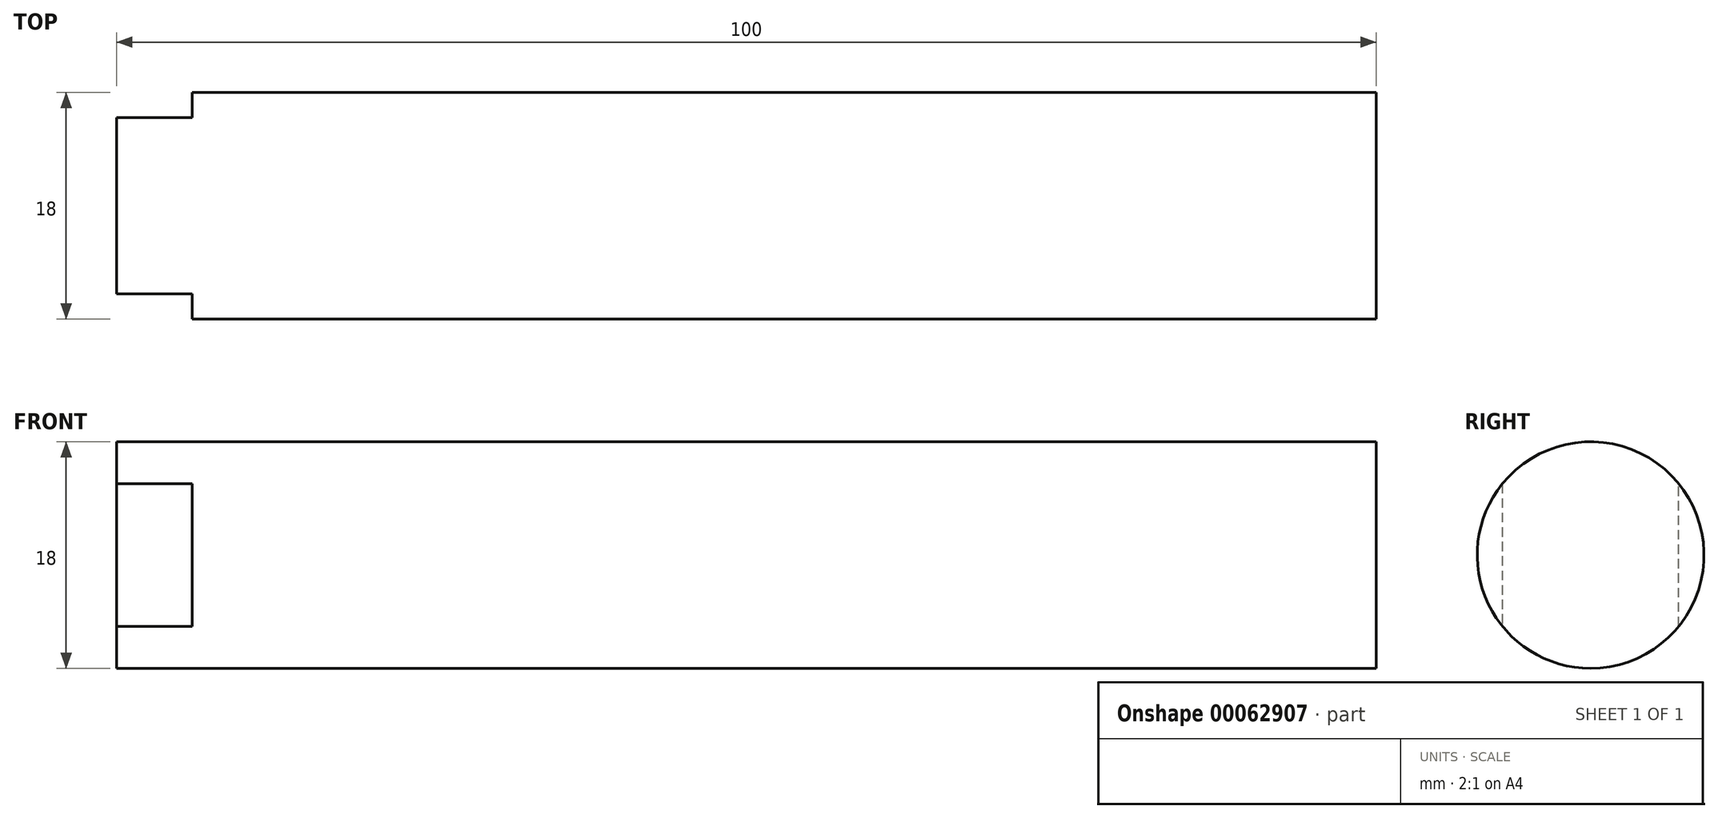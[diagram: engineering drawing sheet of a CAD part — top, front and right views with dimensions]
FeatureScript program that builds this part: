
annotation { "Feature Type Name" : "Feature", "Feature Type Description" : "" }
export const myFeature = defineFeature(function(context is Context, id is Id, definition is map)
    precondition{}
    {
        {
            var Q0;
            Q0=qCreatedBy(makeId("Right.planeOp"),FACE);
            var sketch = newSketch(context, id + "F0", { "sketchPlane" : qUnion([Q0])});
            skCircle(sketch, "E0", {"center": v(0, 0) * mm, "radius": 9 * mm});
            skSolve(sketch);
        }
        {
            var Q0;
            Q0 = qSketchRegion(id + "F0", true);
            extrude(context, id + "F1", {"entities" : qUnion([Q0]), "depth" : 100 * mm});
        }
        {
            var Q0;
            Q0=qCreatedBy(makeId("Right.planeOp"),FACE);
            var sketch = newSketch(context, id + "F2", { "sketchPlane" : qUnion([Q0])});
            skLineSegment(sketch, "E1.bottom", {"start": v(9, 29.91) * mm, "end": v(7, 29.91) * mm});
            skLineSegment(sketch, "E1.top", {"start": v(9, -30.44) * mm, "end": v(7, -30.44) * mm});
            skLineSegment(sketch, "E1.left", {"start": v(9, 29.91) * mm, "end": v(9, -30.44) * mm});
            skLineSegment(sketch, "E1.right", {"start": v(7, 29.91) * mm, "end": v(7, -30.44) * mm});
            skLineSegment(sketch, "E2.bottom", {"start": v(-7, -31.85) * mm, "end": v(-9, -31.85) * mm});
            skLineSegment(sketch, "E2.top", {"start": v(-7, 30.45) * mm, "end": v(-9, 30.45) * mm});
            skLineSegment(sketch, "E2.left", {"start": v(-7, -31.85) * mm, "end": v(-7, 30.45) * mm});
            skLineSegment(sketch, "E2.right", {"start": v(-9, -31.85) * mm, "end": v(-9, 30.45) * mm});
            skSolve(sketch);
        }
        {
            var Q0;
            Q0=makeQuery(id+"F2.imprint","IMPRINT",FACE,{"disambiguationData":[TD([[makeQuery(id+"F2.imprint","IMPRINT",EDGE,{"derivedFrom":sQuery(id+"F2.wireOp",EDGE,"E2.bottom")}),-1.0]])]});
            var Q1;
            Q1=makeQuery(id+"F2.imprint","IMPRINT",FACE,{"disambiguationData":[TD([[makeQuery(id+"F2.imprint","IMPRINT",EDGE,{"derivedFrom":sQuery(id+"F2.wireOp",EDGE,"E1.bottom")}),1.0]])]});
            extrude(context, id + "F3", {"entities" : qUnion([Q0, Q1]), "operationType" : NewBodyOperationType.REMOVE, "endBound" : BoundingType.SYMMETRIC, "depth" : 12 * mm});
        }
    });
